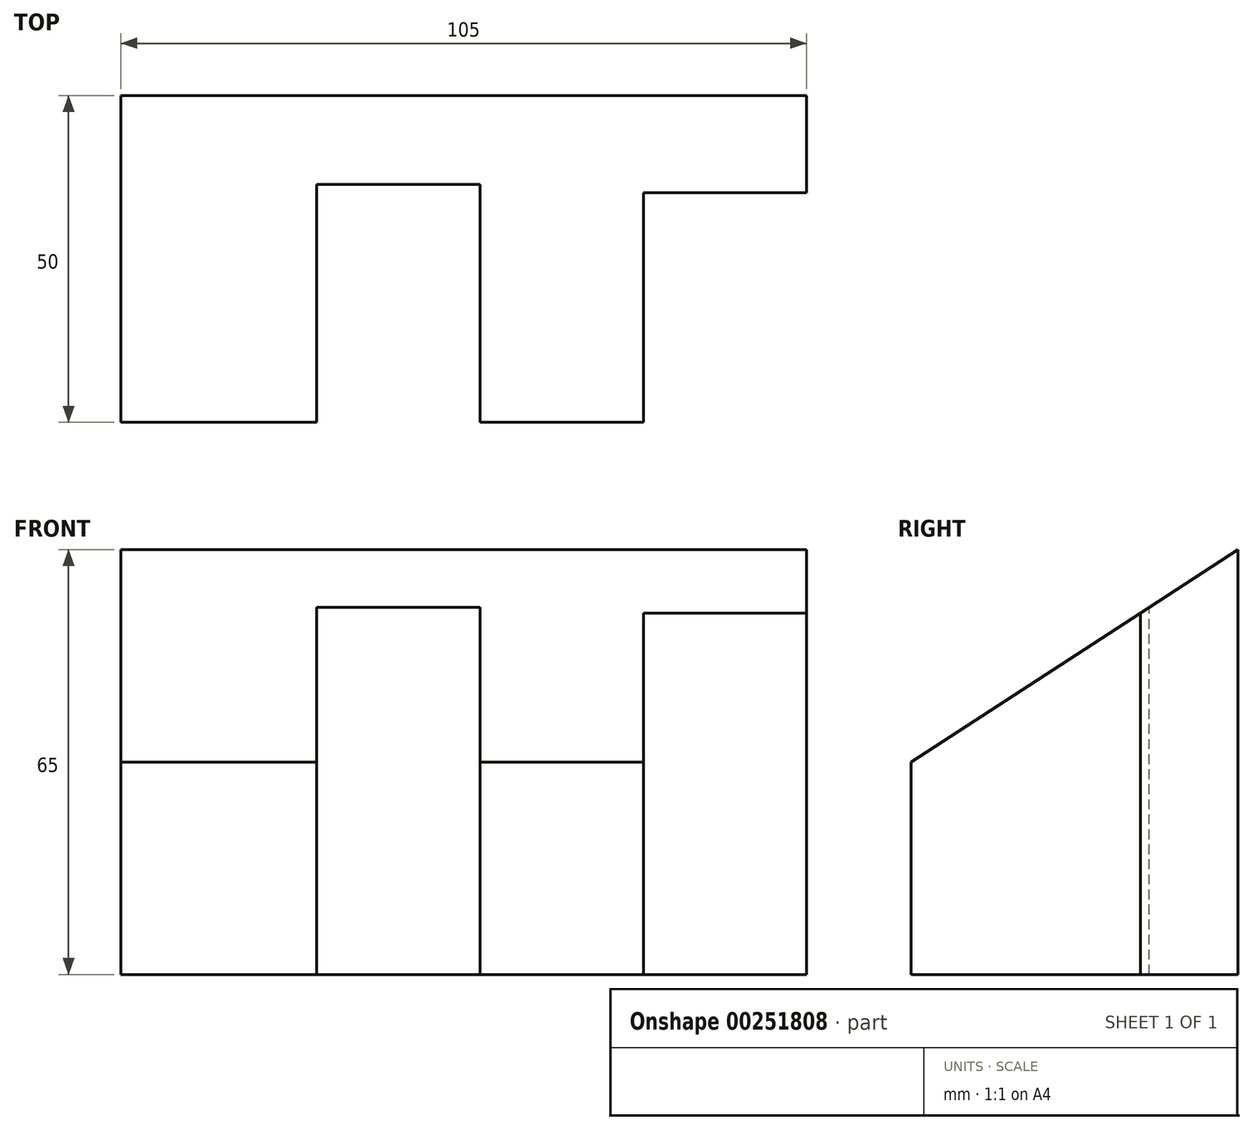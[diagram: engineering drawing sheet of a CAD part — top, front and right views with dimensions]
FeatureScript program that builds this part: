
annotation { "Feature Type Name" : "Feature", "Feature Type Description" : "" }
export const myFeature = defineFeature(function(context is Context, id is Id, definition is map)
    precondition{}
    {
        {
            var Q0;
            Q0=qCreatedBy(makeId("Front.planeOp"),FACE);
            var sketch = newSketch(context, id + "F0", { "sketchPlane" : qUnion([Q0])});
            skLineSegment(sketch, "E0.bottom", {"start": v(-52.5, 32.5) * mm, "end": v(52.5, 32.5) * mm});
            skLineSegment(sketch, "E0.top", {"start": v(-52.5, -32.5) * mm, "end": v(52.5, -32.5) * mm});
            skLineSegment(sketch, "E0.left", {"start": v(-52.5, 32.5) * mm, "end": v(-52.5, -32.5) * mm});
            skLineSegment(sketch, "E0.right", {"start": v(52.5, 32.5) * mm, "end": v(52.5, -32.5) * mm});
            skPoint(sketch, "E0.middle", {"position": v(0, 0) * mm});
            skSolve(sketch);
        }
        {
            var Q0;
            Q0 = qSketchRegion(id + "F0", true);
            extrude(context, id + "F1", {"entities" : qUnion([Q0]), "oppositeDirection" : true, "depth" : 50 * mm});
        }
        {
            var Q0;
            Q0=makeQuery(id+"F1.opExtrude","SWEPT_FACE",FACE,{"disambiguationData":[OSD([sQuery(id+"F0.wireOp",EDGE,"E0.bottom")])]});
            var sketch = newSketch(context, id + "F2", { "sketchPlane" : qUnion([Q0])});
            skLineSegment(sketch, "E1", {"start": v(52.5, 35.1) * mm, "end": v(27.5, 35.1) * mm});
            skLineSegment(sketch, "E2", {"start": v(27.5, 35.1) * mm, "end": v(27.5, 0) * mm});
            skLineSegment(sketch, "E3", {"start": v(27.5, 0) * mm, "end": v(2.5, 0) * mm});
            skLineSegment(sketch, "E4", {"start": v(2.5, 0) * mm, "end": v(2.5, 36.4) * mm});
            skLineSegment(sketch, "E5", {"start": v(2.5, 36.4) * mm, "end": v(-22.5, 36.4) * mm});
            skLineSegment(sketch, "E6", {"start": v(-22.5, 36.4) * mm, "end": v(-22.5, 0) * mm});
            skSolve(sketch);
        }
        {
            var Q0;
            Q0 = qSketchRegion(id + "F2", true);
            var Q1;
            {var subQ0=sQuery(id+"F2.wireOp",EDGE,"E1");Q1=makeQuery(id+"F2.imprint","IMPRINT",FACE,{"disambiguationData":[TD([[makeQuery(id+"F2.imprint","IMPRINT",EDGE,{"derivedFrom":subQ0}),1.0]])]});}
            var Q2;
            {var subQ0=sQuery(id+"F2.wireOp",EDGE,"E4");Q2=makeQuery(id+"F2.imprint","IMPRINT",FACE,{"disambiguationData":[TD([[makeQuery(id+"F2.imprint","IMPRINT",EDGE,{"derivedFrom":subQ0}),1.0]])]});}
            extrude(context, id + "F3", {"entities" : qUnion([Q0, Q1, Q2]), "operationType" : NewBodyOperationType.REMOVE, "oppositeDirection" : true, "depth" : 65 * mm});
        }
        {
            var Q0;
            Q0=makeQuery(id+"F1.opExtrude","SWEPT_FACE",FACE,{"disambiguationData":[OSD([sQuery(id+"F0.wireOp",EDGE,"E0.left")])]});
            var sketch = newSketch(context, id + "F4", { "sketchPlane" : qUnion([Q0])});
            skLineSegment(sketch, "E7", {"start": v(-50, 32.5) * mm, "end": v(0, 0) * mm});
            skLineSegment(sketch, "E8.0.0", {"start": v(0, 0) * mm, "end": v(0, 32.5) * mm});
            skLineSegment(sketch, "E8.0.1", {"start": v(0, 32.5) * mm, "end": v(-50, 32.5) * mm});
            skPoint(sketch, "E8.0.3.start.orphan", {"position": v(-50, -32.5) * mm});
            skPoint(sketch, "E9.orphan", {"position": v(0, -32.5) * mm});
            skSolve(sketch);
        }
        {
            var Q0;
            Q0=makeQuery(id+"F4.imprint","IMPRINT",FACE,{"disambiguationData":[TD([[makeQuery(id+"F4.imprint","IMPRINT",EDGE,{"derivedFrom":sQuery(id+"F4.wireOp",EDGE,"E7")}),1.0]])]});
            extrude(context, id + "F5", {"entities" : qUnion([Q0]), "operationType" : NewBodyOperationType.REMOVE, "oppositeDirection" : true, "depth" : 105 * mm});
        }
    });
